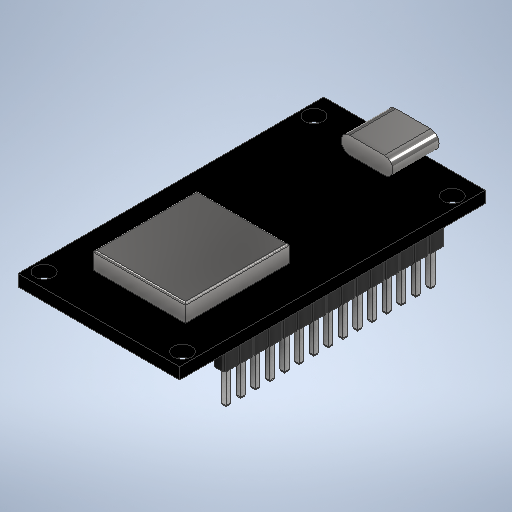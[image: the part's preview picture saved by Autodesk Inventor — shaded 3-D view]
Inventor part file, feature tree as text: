
AUTODESK INVENTOR PART (.ipt)
format: ipt  version: 2025.1 (Build 291241020, 241B)  size: 998,912 bytes
history: native  units: in
note: dims shown in document units (in); Inventor stores cm internally (conversion verified against a paired STEP export)
features: sketch x9, projected_geometry x9, extrude x8, plane x3, pattern_linear x3, fillet x2, mirror x2, chamfer x1
ambient origin geometry x8: Origin, YZ Plane, XZ Plane, XY Plane, X Axis, Y Axis, Z Axis, Center Point
bodies: Solid1 (feature_tree)
feature tree (37):
  extrude  "Extrusion1"  Depth=1.1024in
  extrude  "Extrusion2"  Depth=0.6299in
  fillet  "Fillet1"  Radius=0.7087in
  extrude  "Extrusion3"  Depth=0.1181in TaperAngle=0.0deg
  extrude  "Extrusion5"  Depth=0.3543in
  extrude  "Extrusion6"  Depth=0.013in
  plane  "Work Plane1"
  extrude  "Extrusion7"  Depth=0.126in
  extrude  "Extrusion8"  Depth=0.126in
  chamfer  "Chamfer1"  [1 undecoded]
  fillet  "Fillet2"  Radius=0.0787in
  pattern_linear  "Rectangular Pattern1"  Spacing1=1.4961in  [1 undecoded]
  extrude  "Extrusion9"  Depth=0.0079in
  plane  "Work Plane3"
  mirror  "Mirror2"
  pattern_linear  "Rectangular Pattern2"  Spacing1=0.315in  [1 undecoded]
  pattern_linear  "Rectangular Pattern3"  Spacing1=0.1181in  [1 undecoded]
  mirror  "Mirror3"
  sketch  "Sketch12"  dims[d21=1.9685in d28=0.0in d29=0.0in d30=0.0787in d31=1.4961in d32=0.0079in d33=0.315in d34=0.1181in d35=0.0in d36=0.2559in d37=0.0in d38=0.0394in d39=0.0in d40=0.0315in d41=0.0315in d42=0.0354in d43=0.2362in d44=0.0in d45=0.0039in d46=0.0118in d47=45.0deg d48=0.0039in d49=5.9055in d51=0.0996in d52=0.0118in d53=0.0157in d54=45.0deg d55=0.2362in d56=0.0in d57=5.9055in d59=0.0996in d60=0.7874in d62=0.0996in d63=0.5512in d64=0.6299in d65=0.2953in d66=0.2559in d67=2.0866in d68=1.1024in d69=0.1575in d70=0.1772in d72=0.1575in]
  sketch  "Sketch1"  dims[d0=2.0866in d1=1.1024in]
  sketch  "Sketch2"  dims[d2=0.0787in d3=0.0in d4=0.6299in d5=0.7087in]
  projected_geometry  "Projected Loop1"
  sketch  "Sketch3"  dims[d6=0.2756in d7=0.1181in d8=0.0in]
  projected_geometry  "Projected Loop2"
  sketch  "Sketch5"  dims[d9=0.0118in d10=0.3543in]
  projected_geometry  "Projected Loop3"
  sketch  "Sketch6"  dims[d11=0.1181in d12=0.013in]
  sketch  "Sketch9"  dims[d13=0.0591in d14=0.0in d17=0.126in]
  projected_geometry  "Projected Loop4"
  sketch  "Sketch10"  dims[d18=0.126in d19=0.126in]
  projected_geometry  "Projected Loop5"
  sketch  "Sketch11"  dims[d20=0.126in]
  projected_geometry  "Projected Loop6"
  projected_geometry  "Projected Loop7"
  projected_geometry  "Projected Loop8"
  plane  "Work Plane4"
  projected_geometry  "Projected Loop9"
note: 4 required parameter values undecoded (feature->parameter linkage not recoverable at this tier; creation-order binding heuristic only, values carry confidence <= 0.55)
